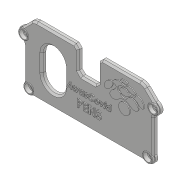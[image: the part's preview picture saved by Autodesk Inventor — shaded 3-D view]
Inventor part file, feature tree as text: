
AUTODESK INVENTOR PART (.ipt)
format: ipt  version: 2017.3 (Build 213257000, 257)  size: 2,940,416 bytes
history: native  units: mm
features: projected_geometry x8, extrude x7, sketch x7, other x6, reference x2, fillet x1
ambient origin geometry x8: Origin, YZ Plane, XZ Plane, XY Plane, X Axis, Y Axis, Z Axis, Center Point
bodies: Solid1 (feature_tree)
feature tree (31):
  other  "Cover Flir One Pro.ipt"
  extrude  "Extrusion1"  Depth=1.275mm TaperAngle=0.0deg
  extrude  "Extrusion2"  Depth=7.0mm
  extrude  "Extrusion3"  Depth=0.55mm TaperAngle=0.0deg
  extrude  "Extrusion4"  Depth=0.2mm
  fillet  "Fillet1"  Radius=10.0mm
  extrude  "Extrusion6"  Depth=0.5mm TaperAngle=0.0deg
  extrude  "Extrusion7"  [1 undecoded]
  extrude  "Extrusion8"  [1 undecoded]
  other  "Solid3::Cover Flir One Pro.ipt"
  other  "TaggingFeature1"
  sketch  "Sketch1"  dims[d0=10.0mm d1=1.275mm d2=0.0mm]
  reference  "Reference1"
  reference  "Reference2"
  sketch  "Sketch2"  dims[d3=7.0mm d4=7.0mm]
  sketch  "Sketch3"  dims[d5=10.0mm d6=0.0mm d7=0.55mm d8=0.0mm]
  projected_geometry  "Projected Loop1"
  projected_geometry  "Projected Loop2"
  projected_geometry  "Projected Loop3"
  projected_geometry  "Projected Loop4"
  projected_geometry  "Projected Loop5"
  projected_geometry  "Projected Loop6"
  sketch  "Sketch4"  dims[d9=0.0mm d10=0.0mm d13=0.2mm d14=10.0mm d15=0.0mm]
  projected_geometry  "Projected Loop7"
  sketch  "Sketch6"  dims[d19=0.5mm d20=0.0mm d22=0.5mm d23=0.0mm]
  projected_geometry  "Projected Loop8"
  sketch  "Sketch7"
  sketch  "Sketch8"
  parser-record x1  (decoder bookkeeping rows leaked as tree rows — omitted from the tree; the rows remain in map.json)
  other  "Assembly1.iam"
  other  "CoverPart1:1"
note: 2 required parameter values undecoded (feature->parameter linkage not recoverable at this tier; creation-order binding heuristic only, values carry confidence <= 0.55)
note: 1 file-system path scrubbed to <path> (originals preserved in map.json)
